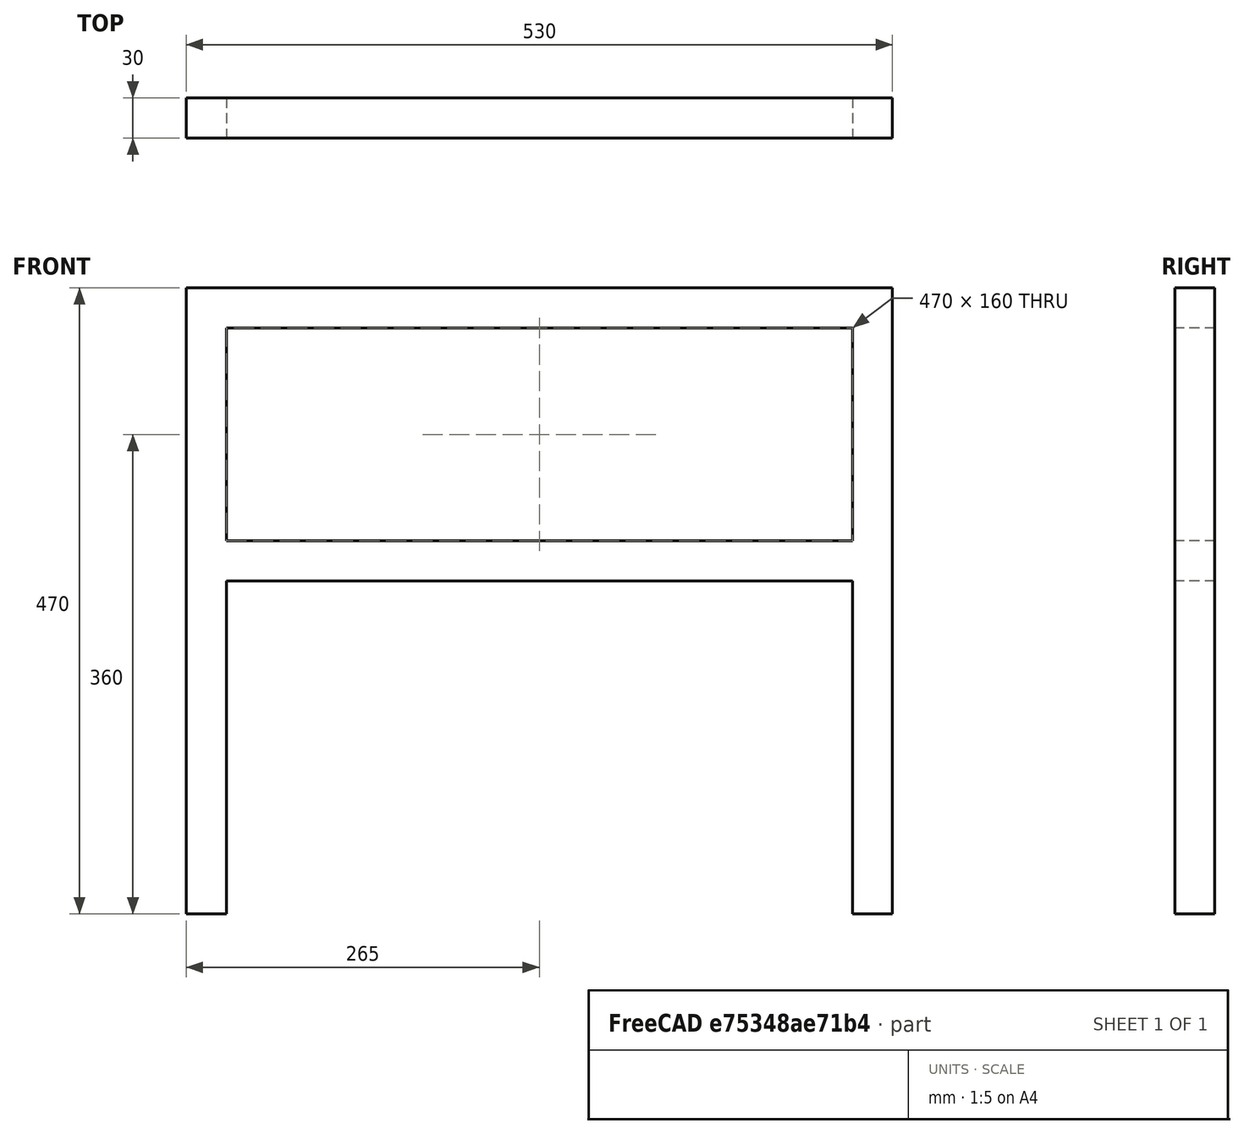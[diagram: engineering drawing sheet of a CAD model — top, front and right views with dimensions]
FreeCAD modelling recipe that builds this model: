
FCSTD DOCUMENT  (FreeCAD 0.16R6348 (Git))
Label: Puente
License: All rights reserved
LicenseURL: http://es.wikipedia.org/wiki/Todos_los_derechos_reservados
objects: Sketcher::SketchObject×1, PartDesign::Pad×1, Part::Feature×1
note: 4 computed .brp shape members not serialized (recipe doc carries the construction recipe); baked Part::Feature solids carry a one-line shape summary decoded from their .brp

FEATURE [Sketcher::SketchObject] Sketch
  Placement = pos=(0,0,0) rot=(-1,0,0;4.71239rad)
  sketch-geometry (12):
    g0: LineSegment StartX=0 StartY=0 StartZ=0 EndX=30 EndY=0 EndZ=0
    g1: LineSegment StartX=0 StartY=0 StartZ=0 EndX=0 EndY=470 EndZ=0
    g2: LineSegment StartX=0 StartY=470 StartZ=0 EndX=530 EndY=470 EndZ=0
    g3: LineSegment StartX=530 StartY=470 StartZ=0 EndX=530 EndY=0 EndZ=0
    g4: LineSegment StartX=530 StartY=0 StartZ=0 EndX=500 EndY=0 EndZ=0
    g5: LineSegment StartX=500 StartY=0 StartZ=0 EndX=500 EndY=250 EndZ=0
    g6: LineSegment StartX=500 StartY=250 StartZ=0 EndX=30 EndY=250 EndZ=0
    g7: LineSegment StartX=30 StartY=250 StartZ=0 EndX=30 EndY=0 EndZ=0
    g8: LineSegment StartX=30 StartY=440 StartZ=0 EndX=500 EndY=440 EndZ=0
    g9: LineSegment StartX=500 StartY=440 StartZ=0 EndX=500 EndY=280 EndZ=0
    g10: LineSegment StartX=500 StartY=280 StartZ=0 EndX=30 EndY=280 EndZ=0
    g11: LineSegment StartX=30 StartY=280 StartZ=0 EndX=30 EndY=440 EndZ=0
  constraints (35):
    c: Coincident(g-1,g0)
    c: Horizontal(g0)
    c: Coincident(g-1,g1)
    c: Vertical(g1)
    c: Coincident(g1,g2)
    c: Horizontal(g2)
    c: Coincident(g2,g3)
    c: Vertical(g3)
    c: Coincident(g3,g4)
    c: Coincident(g4,g5)
    c: Vertical(g5)
    c: Coincident(g5,g6)
    c: Coincident(g6,g7)
    c: Coincident(g7,g0)
    c: Vertical(g7)
    c: Horizontal(g4)
    c: Horizontal(g6)
    c: Equal(g0,g4)
    c: DistanceX(g-1,g0) = 30
    c: DistanceY(g-1,g1) = 470
    c: DistanceX(g1,g2) = 530
    c: Coincident(g8,g9)
    c: Coincident(g9,g10)
    c: Coincident(g10,g11)
    c: Coincident(g11,g8)
    c: Horizontal(g8)
    c: Horizontal(g10)
    c: Vertical(g9)
    c: Vertical(g11)
    c: DistanceX(g-1,g10) = 30
    c: DistanceY(g8,g1) = 30
    c: DistanceY(g10,g6) = -30
    c: DistanceX(g9,g3) = 30
    c: DistanceY(g0,g6) = 250
    c: Equal(g7,g5)
FEATURE [PartDesign::Pad] Pad
  Length = 30
  Length2 = 100
  Placement = pos=(0,0,0) rot=(-1,0,0;4.71239rad)
  Sketch = -> Sketch
  Type = 0
FEATURE [Part::Feature] Pad001
  Placement = pos=(0,0,0) rot=(1,0,0;1.5708rad)
  shape: bbox 530 x 30 x 470 mm, 14 faces (baked)
